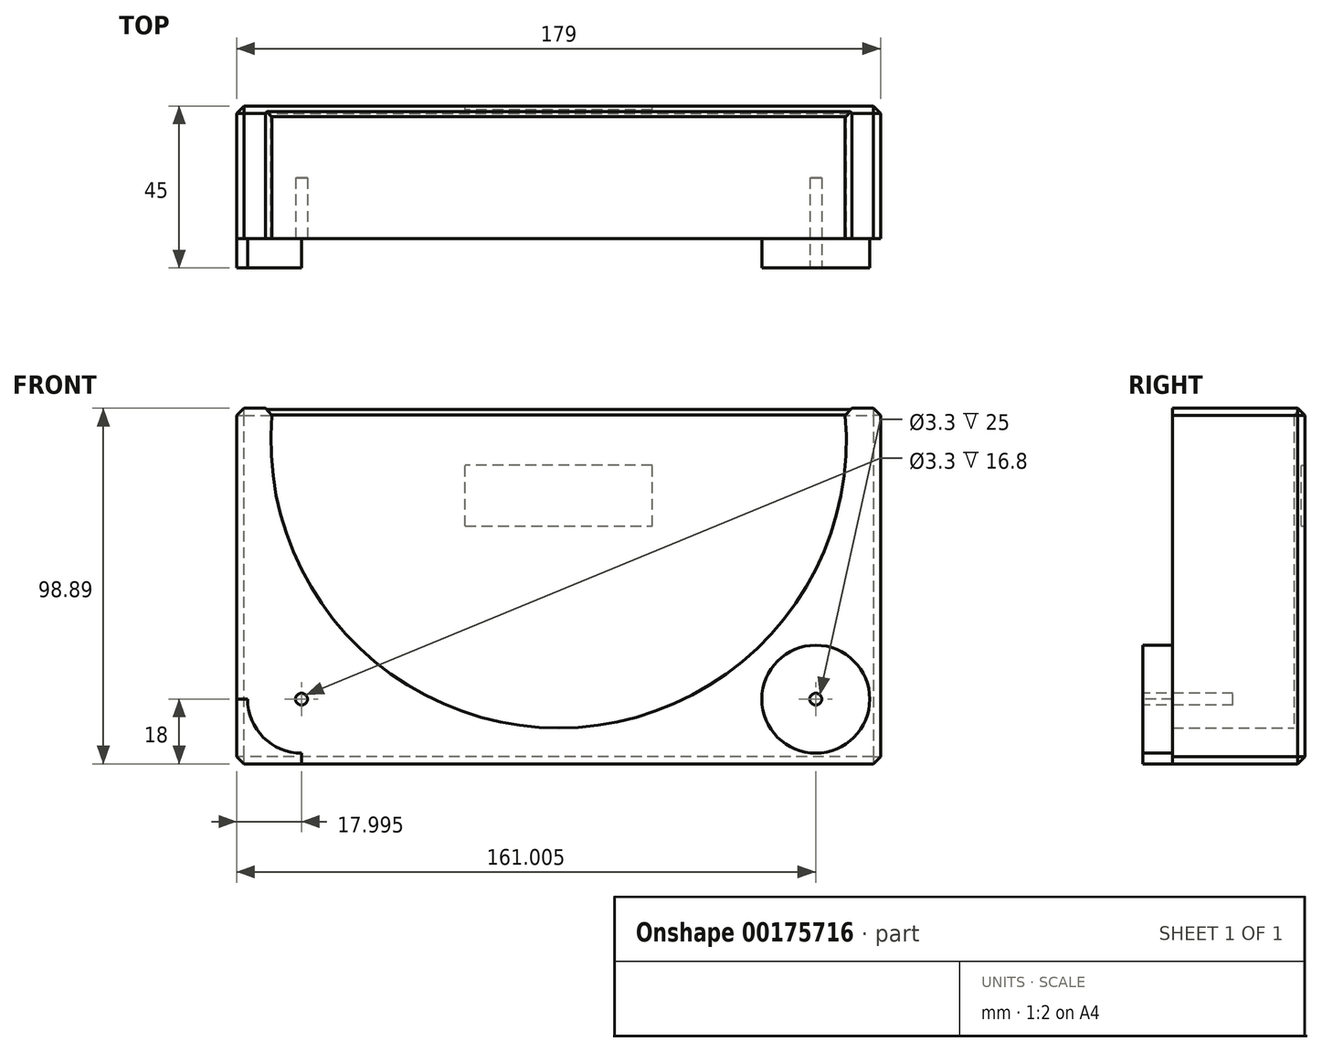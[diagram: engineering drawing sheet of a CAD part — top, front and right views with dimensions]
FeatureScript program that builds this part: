
annotation { "Feature Type Name" : "Feature", "Feature Type Description" : "" }
export const myFeature = defineFeature(function(context is Context, id is Id, definition is map)
    precondition{}
    {
        {
            var Q0;
            Q0=qCreatedBy(makeId("Front.planeOp"),FACE);
            var sketch = newSketch(context, id + "F0", { "sketchPlane" : qUnion([Q0])});
            skCircle(sketch, "E0", {"center": v(0, 90) * mm, "radius": 80 * mm});
            skLineSegment(sketch, "E1", {"start": v(-79.5, 98.89) * mm, "end": v(-89.5, 98.89) * mm});
            skLineSegment(sketch, "E2", {"start": v(-89.5, 98.89) * mm, "end": v(-89.5, 0) * mm});
            skLineSegment(sketch, "E3", {"start": v(-89.5, 0) * mm, "end": v(0, 0) * mm});
            skLineSegment(sketch, "E4.MirrorCS", {"start": v(79.5, 98.89) * mm, "end": v(89.5, 98.89) * mm});
            skLineSegment(sketch, "E5.MirrorCS", {"start": v(89.5, 98.89) * mm, "end": v(89.5, 0) * mm});
            skLineSegment(sketch, "E6.MirrorCS", {"start": v(89.5, 0) * mm, "end": v(0, 0) * mm});
            skLineSegment(sketch, "E7", {"start": v(79.5, 98.89) * mm, "end": v(-79.5, 98.89) * mm});
            skLineSegment(sketch, "E8", {"start": v(0, 66.09) * mm, "end": v(26, 66.09) * mm});
            skLineSegment(sketch, "E9", {"start": v(26, 66.09) * mm, "end": v(26, 83.09) * mm});
            skLineSegment(sketch, "E10", {"start": v(26, 83.09) * mm, "end": v(0, 83.09) * mm});
            skLineSegment(sketch, "E11", {"start": v(0, 83.09) * mm, "end": v(0, 65.32) * mm});
            skLineSegment(sketch, "E12.MirrorCS", {"start": v(-26, 83.09) * mm, "end": v(0, 83.09) * mm});
            skLineSegment(sketch, "E13.MirrorCS", {"start": v(-26, 66.09) * mm, "end": v(-26, 83.09) * mm});
            skLineSegment(sketch, "E14.MirrorCS", {"start": v(0, 66.09) * mm, "end": v(-26, 66.09) * mm});
            skLineSegment(sketch, "E15", {"start": v(0, 83.09) * mm, "end": v(0, 98.89) * mm});
            skSolve(sketch);
        }
        {
            var Q0;
            {var subQ0=sQuery(id+"F0.wireOp",EDGE,"E1");Q0=makeQuery(id+"F0.imprint","IMPRINT",FACE,{"disambiguationData":[TD([[makeQuery(id+"F0.imprint","IMPRINT",EDGE,{"derivedFrom":subQ0}),1.0]])]});}
            extrude(context, id + "F1", {"entities" : qUnion([Q0]), "depth" : 45 * mm});
        }
        {
            var Q0;
            Q0=makeQuery(id+"F1.opExtrude","CAP_FACE",FACE,{"disambiguationData":[OSD([sQuery(id+"F0.wireOp",EDGE,"E0"),sQuery(id+"F0.wireOp",EDGE,"E1"),sQuery(id+"F0.wireOp",EDGE,"E2"),sQuery(id+"F0.wireOp",EDGE,"E3"),sQuery(id+"F0.wireOp",EDGE,"E4.MirrorCS"),sQuery(id+"F0.wireOp",EDGE,"E5.MirrorCS"),sQuery(id+"F0.wireOp",EDGE,"E6.MirrorCS")])],"isStart":false});
            var sketch = newSketch(context, id + "F2", { "sketchPlane" : qUnion([Q0])});
            skLineSegment(sketch, "E16", {"start": v(-89.5, 98.89) * mm, "end": v(89.5, 98.89) * mm});
            skLineSegment(sketch, "E17", {"start": v(89.5, 98.89) * mm, "end": v(89.5, 0) * mm});
            skLineSegment(sketch, "E18", {"start": v(89.5, 0) * mm, "end": v(-89.5, 0) * mm});
            skLineSegment(sketch, "E19", {"start": v(-89.5, 0) * mm, "end": v(-89.5, 98.89) * mm});
            skLineSegment(sketch, "E20", {"start": v(-89.5, 18) * mm, "end": v(-71.5, 18) * mm});
            skLineSegment(sketch, "E21", {"start": v(-71.5, 18) * mm, "end": v(-71.5, 0) * mm});
            skCircle(sketch, "E22", {"center": v(-71.5, 18) * mm, "radius": 15 * mm});
            skLineSegment(sketch, "E23", {"start": v(0, 0) * mm, "end": v(0, 4.98) * mm});
            skCircle(sketch, "E24.MirrorC", {"center": v(71.5, 18) * mm, "radius": 15 * mm});
            skCircle(sketch, "E25", {"center": v(-71.5, 18) * mm, "radius": 1.65 * mm});
            skCircle(sketch, "E26", {"center": v(71.5, 18) * mm, "radius": 1.65 * mm});
            skSolve(sketch);
        }
        {
            var Q0;
            {var subQ0=sQuery(id+"F0.wireOp",EDGE,"E7");Q0=makeQuery(id+"F0.imprint","IMPRINT",FACE,{"disambiguationData":[TD([[makeQuery(id+"F0.imprint","IMPRINT",EDGE,{"derivedFrom":subQ0}),1.0]])]});}
            var Q1;
            Q1=makeQuery(id+"F0.imprint","IMPRINT",FACE,{"disambiguationData":[TD([[makeQuery(id+"F0.imprint","IMPRINT",EDGE,{"derivedFrom":sQuery(id+"F0.wireOp",EDGE,"E8")}),1.0]])]});
            var Q2;
            {var subQ2=sQuery(id+"F0.wireOp",EDGE,"E12.MirrorCS");Q2=makeQuery(id+"F0.imprint","IMPRINT",FACE,{"disambiguationData":[TD([[makeQuery(id+"F0.imprint","IMPRINT",EDGE,{"derivedFrom":subQ2}),-1.0]])]});}
            extrude(context, id + "F3", {"entities" : qUnion([Q0, Q1, Q2]), "operationType" : NewBodyOperationType.ADD, "depth" : 3 * mm});
        }
        {
            var Q0;
            {var subQ1=makeQuery(id+"F1.opExtrude","CAP_EDGE",EDGE,{"disambiguationData":[OSD([sQuery(id+"F0.wireOp",EDGE,"E0")])],"isStart":false});Q0=makeQuery(id+"F2.imprint","IMPRINT",FACE,{"disambiguationData":[TD([[makeQuery(id+"F2.imprint","IMPRINT",EDGE,{"derivedFrom":subQ1}),1.0]])]});}
            var Q1;
            Q1=makeQuery(id+"F2.imprint","IMPRINT",FACE,{"disambiguationData":[TD([[makeQuery(id+"F2.imprint","IMPRINT",EDGE,{"derivedFrom":sQuery(id+"F2.wireOp",EDGE,"E24.MirrorC")}),-1.0]])]});
            var Q2;
            {var subQ0=sQuery(id+"F2.wireOp",EDGE,"E22");var subQ1=sQuery(id+"F2.wireOp",EDGE,"E20");var subQ2=makeQuery(id+"F2.imprint","INTERSECT",VERTEX,{"derivedFrom":[subQ1,subQ0]});Q2=makeQuery(id+"F2.imprint","IMPRINT",FACE,{"disambiguationData":[TD([[makeQuery(id+"F2.imprint","IMPRINT",EDGE,{"disambiguationData":[TD([[subQ2,-1.0]])],"derivedFrom":subQ1}),1.0]])]});}
            var Q3;
            {var subQ0=sQuery(id+"F2.wireOp",EDGE,"E22");var subQ1=sQuery(id+"F2.wireOp",EDGE,"E20");var subQ2=makeQuery(id+"F2.imprint","INTERSECT",VERTEX,{"derivedFrom":[subQ1,subQ0]});Q3=makeQuery(id+"F2.imprint","IMPRINT",FACE,{"disambiguationData":[TD([[makeQuery(id+"F2.imprint","IMPRINT",EDGE,{"disambiguationData":[TD([[subQ2,-1.0]])],"derivedFrom":subQ1}),-1.0]])]});}
            extrude(context, id + "F4", {"entities" : qUnion([Q0, Q1, Q2, Q3]), "operationType" : NewBodyOperationType.REMOVE, "oppositeDirection" : true, "depth" : 8.2 * mm});
        }
        {
            var Q0;
            Q0=makeQuery(id+"F2.imprint","IMPRINT",FACE,{"disambiguationData":[TD([[makeQuery(id+"F2.imprint","IMPRINT",EDGE,{"derivedFrom":sQuery(id+"F2.wireOp",EDGE,"E26")}),1.0]])]});
            var Q1;
            {var subQ0=sQuery(id+"F2.wireOp",EDGE,"E21");var subQ1=sQuery(id+"F2.wireOp",EDGE,"E20");var subQ2=makeQuery(id+"F2.imprint","INTERSECT",VERTEX,{"derivedFrom":[subQ1,subQ0]});Q1=makeQuery(id+"F2.imprint","IMPRINT",FACE,{"disambiguationData":[TD([[makeQuery(id+"F2.imprint","IMPRINT",EDGE,{"disambiguationData":[TD([[subQ2,1.0]])],"derivedFrom":subQ1}),1.0]])]});}
            var Q2;
            {var subQ0=sQuery(id+"F2.wireOp",EDGE,"E21");var subQ1=sQuery(id+"F2.wireOp",EDGE,"E20");var subQ2=makeQuery(id+"F2.imprint","INTERSECT",VERTEX,{"derivedFrom":[subQ1,subQ0]});Q2=makeQuery(id+"F2.imprint","IMPRINT",FACE,{"disambiguationData":[TD([[makeQuery(id+"F2.imprint","IMPRINT",EDGE,{"disambiguationData":[TD([[subQ2,1.0]])],"derivedFrom":subQ1}),-1.0]])]});}
            var Q3;
            Q3=sQuery(id+"F2.wireOp",EDGE,"E26");
            var Q4;
            Q4=sQuery(id+"F2.wireOp",EDGE,"E25");
            extrude(context, id + "F5", {"entities" : qUnion([Q0, Q1, Q2]), "operationType" : NewBodyOperationType.REMOVE, "surfaceEntities" : qUnion([Q3, Q4]), "oppositeDirection" : true, "depth" : 25 * mm});
        }
        {
            var Q0;
            Q0=makeQuery(id+"F0.imprint","IMPRINT",FACE,{"disambiguationData":[TD([[makeQuery(id+"F0.imprint","IMPRINT",EDGE,{"derivedFrom":sQuery(id+"F0.wireOp",EDGE,"E8")}),1.0]])]});
            var Q1;
            {var subQ2=sQuery(id+"F0.wireOp",EDGE,"E12.MirrorCS");Q1=makeQuery(id+"F0.imprint","IMPRINT",FACE,{"disambiguationData":[TD([[makeQuery(id+"F0.imprint","IMPRINT",EDGE,{"derivedFrom":subQ2}),-1.0]])]});}
            extrude(context, id + "F6", {"entities" : qUnion([Q0, Q1]), "operationType" : NewBodyOperationType.REMOVE, "depth" : 1 * mm});
        }
        {
            var Q0;
            Q0=makeQuery(id+"F1.opExtrude","SWEPT_EDGE",EDGE,{"disambiguationData":[OSD([sQuery(id+"F0.wireOp",EDGE,"E0"),sQuery(id+"F0.wireOp",EDGE,"E1"),sQuery(id+"F0.wireOp",EDGE,"E7")])]});
            var Q1;
            Q1=makeQuery(id+"F3.boolean.opBoolean","MERGE",EDGE,{"derivedFrom":[makeQuery(id+"F1.opExtrude","CAP_EDGE",EDGE,{"disambiguationData":[OSD([sQuery(id+"F0.wireOp",EDGE,"E1")])],"isStart":true}),makeQuery(id+"F1.opExtrude","CAP_EDGE",EDGE,{"disambiguationData":[OSD([sQuery(id+"F0.wireOp",EDGE,"E4.MirrorCS")])],"isStart":true}),makeQuery(id+"F3.opExtrude","CAP_EDGE",EDGE,{"disambiguationData":[OSD([sQuery(id+"F0.wireOp",EDGE,"E7")])],"isStart":true})]});
            var Q2;
            Q2=makeQuery(id+"F3.opExtrude","CAP_EDGE",EDGE,{"disambiguationData":[OSD([sQuery(id+"F0.wireOp",EDGE,"E7")])],"isStart":false});
            var Q3;
            Q3=makeQuery(id+"F1.opExtrude","CAP_EDGE",EDGE,{"disambiguationData":[OSD([sQuery(id+"F0.wireOp",EDGE,"E2")])],"isStart":true});
            var Q4;
            Q4=makeQuery(id+"F1.opExtrude","CAP_EDGE",EDGE,{"disambiguationData":[OSD([sQuery(id+"F0.wireOp",EDGE,"E5.MirrorCS")])],"isStart":true});
            var Q5;
            Q5=makeQuery(id+"F1.opExtrude","SWEPT_EDGE",EDGE,{"disambiguationData":[OSD([sQuery(id+"F0.wireOp",EDGE,"E4.MirrorCS"),sQuery(id+"F0.wireOp",EDGE,"E5.MirrorCS")])]});
            var Q6;
            Q6=makeQuery(id+"F1.opExtrude","SWEPT_EDGE",EDGE,{"disambiguationData":[OSD([sQuery(id+"F0.wireOp",EDGE,"E0"),sQuery(id+"F0.wireOp",EDGE,"E4.MirrorCS"),sQuery(id+"F0.wireOp",EDGE,"E7")])]});
            var Q7;
            Q7=makeQuery(id+"F1.opExtrude","SWEPT_EDGE",EDGE,{"disambiguationData":[OSD([sQuery(id+"F0.wireOp",EDGE,"E1"),sQuery(id+"F0.wireOp",EDGE,"E2")])]});
            var Q8;
            Q8=makeQuery(id+"F1.opExtrude","SWEPT_EDGE",EDGE,{"disambiguationData":[OSD([sQuery(id+"F0.wireOp",EDGE,"E2"),sQuery(id+"F0.wireOp",EDGE,"E3")])]});
            var Q9;
            Q9=makeQuery(id+"F1.opExtrude","CAP_EDGE",EDGE,{"disambiguationData":[OSD([sQuery(id+"F0.wireOp",EDGE,"E3"),sQuery(id+"F0.wireOp",EDGE,"E6.MirrorCS")])],"isStart":true});
            var Q10;
            Q10=makeQuery(id+"F1.opExtrude","SWEPT_EDGE",EDGE,{"disambiguationData":[OSD([sQuery(id+"F0.wireOp",EDGE,"E5.MirrorCS"),sQuery(id+"F0.wireOp",EDGE,"E6.MirrorCS")])]});
            chamfer(context, id + "F7", {"entities" : qUnion([Q0, Q1, Q2, Q3, Q4, Q5, Q6, Q7, Q8, Q9, Q10]), "width" : 2 * mm, "tangentPropagation" : true});
        }
    });
